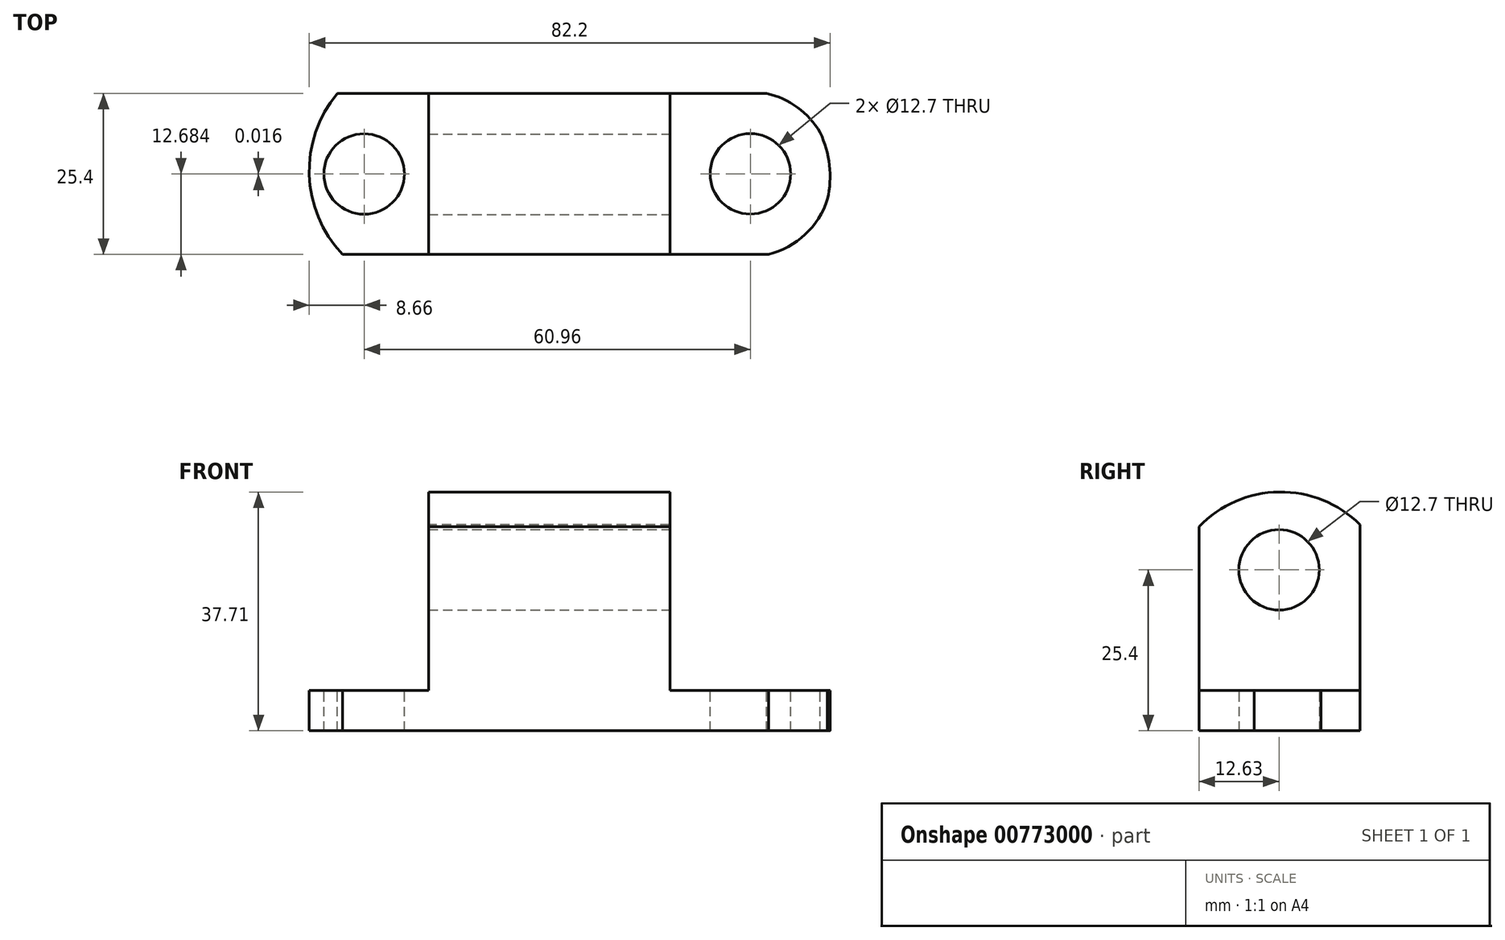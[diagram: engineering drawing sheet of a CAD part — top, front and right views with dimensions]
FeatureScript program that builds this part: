
annotation { "Feature Type Name" : "Feature", "Feature Type Description" : "" }
export const myFeature = defineFeature(function(context is Context, id is Id, definition is map)
    precondition{}
    {
        {
            var Q0;
            Q0=qCreatedBy(makeId("Front.planeOp"),FACE);
            var sketch = newSketch(context, id + "F0", { "sketchPlane" : qUnion([Q0])});
            skLineSegment(sketch, "E0", {"start": v(0, 0) * mm, "end": v(82.55, 0) * mm});
            skLineSegment(sketch, "E1", {"start": v(82.55, 0) * mm, "end": v(82.55, 38.1) * mm});
            skLineSegment(sketch, "E2", {"start": v(82.55, 38.1) * mm, "end": v(0, 38.1) * mm});
            skLineSegment(sketch, "E3", {"start": v(0, 38.1) * mm, "end": v(0, 0) * mm});
            skSolve(sketch);
        }
        {
            var Q0;
            Q0=makeQuery(id+"F0.imprint","IMPRINT",FACE,{"disambiguationData":[TD([[makeQuery(id+"F0.imprint","IMPRINT",EDGE,{"derivedFrom":sQuery(id+"F0.wireOp",EDGE,"E0")}),1.0]])]});
            extrude(context, id + "F1", {"entities" : qUnion([Q0]), "depth" : 25.4 * mm, "offsetDistance" : 25.4 * mm});
        }
        {
            var Q0;
            Q0=makeQuery(id+"F1.opExtrude","CAP_FACE",FACE,{"disambiguationData":[OSD([sQuery(id+"F0.wireOp",EDGE,"E0"),sQuery(id+"F0.wireOp",EDGE,"E1"),sQuery(id+"F0.wireOp",EDGE,"E2"),sQuery(id+"F0.wireOp",EDGE,"E3")])],"isStart":false});
            var sketch = newSketch(context, id + "F2", { "sketchPlane" : qUnion([Q0])});
            skLineSegment(sketch, "E4", {"start": v(57.15, 38.1) * mm, "end": v(57.15, 6.35) * mm});
            skLineSegment(sketch, "E5", {"start": v(57.15, 6.35) * mm, "end": v(82.55, 6.35) * mm});
            skLineSegment(sketch, "E6", {"start": v(82.55, 6.35) * mm, "end": v(82.55, 38.1) * mm});
            skLineSegment(sketch, "E7", {"start": v(82.55, 38.1) * mm, "end": v(57.15, 38.1) * mm});
            skSolve(sketch);
        }
        {
            var Q0;
            Q0=makeQuery(id+"F2.imprint","IMPRINT",FACE,{"disambiguationData":[TD([[makeQuery(id+"F2.imprint","IMPRINT",EDGE,{"derivedFrom":sQuery(id+"F2.wireOp",EDGE,"E4")}),1.0]])]});
            extrude(context, id + "F3", {"entities" : qUnion([Q0]), "operationType" : NewBodyOperationType.REMOVE, "oppositeDirection" : true, "depth" : 25.4 * mm, "offsetDistance" : 25.4 * mm});
        }
        {
            var Q0;
            Q0=makeQuery(id+"F1.opExtrude","CAP_FACE",FACE,{"disambiguationData":[OSD([sQuery(id+"F0.wireOp",EDGE,"E0"),sQuery(id+"F0.wireOp",EDGE,"E1"),sQuery(id+"F0.wireOp",EDGE,"E2"),sQuery(id+"F0.wireOp",EDGE,"E3")])],"isStart":false});
            var sketch = newSketch(context, id + "F4", { "sketchPlane" : qUnion([Q0])});
            skLineSegment(sketch, "E8", {"start": v(19.05, 38.1) * mm, "end": v(19.05, 6.35) * mm});
            skLineSegment(sketch, "E9", {"start": v(19.05, 6.35) * mm, "end": v(0, 6.35) * mm});
            skLineSegment(sketch, "E10", {"start": v(0, 6.35) * mm, "end": v(0, 38.1) * mm});
            skLineSegment(sketch, "E11", {"start": v(0, 38.1) * mm, "end": v(19.05, 38.1) * mm});
            skSolve(sketch);
        }
        {
            var Q0;
            Q0=makeQuery(id+"F4.imprint","IMPRINT",FACE,{"disambiguationData":[TD([[makeQuery(id+"F4.imprint","IMPRINT",EDGE,{"derivedFrom":sQuery(id+"F4.wireOp",EDGE,"E8")}),-1.0]])]});
            extrude(context, id + "F5", {"entities" : qUnion([Q0]), "operationType" : NewBodyOperationType.REMOVE, "oppositeDirection" : true, "depth" : 25.4 * mm, "offsetDistance" : 25.4 * mm});
        }
        {
            var Q0;
            Q0=makeQuery(id+"F3.boolean.opBoolean","COPY",FACE,{"derivedFrom":makeQuery(id+"F3.opExtrude","SWEPT_FACE",FACE,{"disambiguationData":[OSD([sQuery(id+"F2.wireOp",EDGE,"E5")])]})});
            var sketch = newSketch(context, id + "F6", { "sketchPlane" : qUnion([Q0])});
            skCircle(sketch, "E12", {"center": v(69.85, -12.7) * mm, "radius": 6.35 * mm});
            skSolve(sketch);
        }
        {
            var Q0;
            Q0=makeQuery(id+"F6.imprint","IMPRINT",FACE,{"disambiguationData":[TD([[makeQuery(id+"F6.imprint","IMPRINT",EDGE,{"derivedFrom":sQuery(id+"F6.wireOp",EDGE,"E12")}),1.0]])]});
            extrude(context, id + "F7", {"entities" : qUnion([Q0]), "operationType" : NewBodyOperationType.REMOVE, "oppositeDirection" : true, "depth" : 25.4 * mm, "offsetDistance" : 25.4 * mm});
        }
        {
            var Q0;
            Q0=makeQuery(id+"F5.boolean.opBoolean","COPY",FACE,{"derivedFrom":makeQuery(id+"F5.opExtrude","SWEPT_FACE",FACE,{"disambiguationData":[OSD([sQuery(id+"F4.wireOp",EDGE,"E9")])]})});
            var sketch = newSketch(context, id + "F8", { "sketchPlane" : qUnion([Q0])});
            skCircle(sketch, "E13", {"center": v(8.9, -12.72) * mm, "radius": 6.35 * mm});
            skSolve(sketch);
        }
        {
            var Q0;
            Q0=makeQuery(id+"F8.imprint","IMPRINT",FACE,{"disambiguationData":[TD([[makeQuery(id+"F8.imprint","IMPRINT",EDGE,{"derivedFrom":sQuery(id+"F8.wireOp",EDGE,"E13")}),1.0]])]});
            extrude(context, id + "F9", {"entities" : qUnion([Q0]), "operationType" : NewBodyOperationType.REMOVE, "oppositeDirection" : true, "depth" : 25.4 * mm, "offsetDistance" : 25.4 * mm});
        }
        {
            var Q0;
            Q0=makeQuery(id+"F5.boolean.opBoolean","COPY",FACE,{"derivedFrom":makeQuery(id+"F5.opExtrude","SWEPT_FACE",FACE,{"disambiguationData":[OSD([sQuery(id+"F4.wireOp",EDGE,"E8")])]})});
            var sketch = newSketch(context, id + "F10", { "sketchPlane" : qUnion([Q0])});
            skArc(sketch, "E14", {"start": v(25.4, 32.2) * mm, "mid": v(12.77, 37.7) * mm, "end": v(0, 32.54) * mm});
            skSolve(sketch);
        }
        {
            var Q0;
            {var subQ0=sQuery(id+"F10.wireOp",EDGE,"E14");Q0=makeQuery(id+"F10.imprint","IMPRINT",FACE,{"disambiguationData":[TD([[makeQuery(id+"F10.imprint","IMPRINT",EDGE,{"derivedFrom":subQ0}),-1.0]])]});}
            extrude(context, id + "F11", {"entities" : qUnion([Q0]), "operationType" : NewBodyOperationType.REMOVE, "oppositeDirection" : true, "depth" : 38.1 * mm, "offsetDistance" : 25.4 * mm});
        }
        {
            var Q0;
            Q0=makeQuery(id+"F3.boolean.opBoolean","COPY",FACE,{"derivedFrom":makeQuery(id+"F3.opExtrude","SWEPT_FACE",FACE,{"disambiguationData":[OSD([sQuery(id+"F2.wireOp",EDGE,"E4")])]})});
            var sketch = newSketch(context, id + "F12", { "sketchPlane" : qUnion([Q0])});
            skCircle(sketch, "E15", {"center": v(-12.77, 25.4) * mm, "radius": 6.35 * mm});
            skPoint(sketch, "E15.centerSnap0", {"position": v(-12.77, 37.7) * mm});
            skSolve(sketch);
        }
        {
            var Q0;
            Q0=makeQuery(id+"F12.imprint","IMPRINT",FACE,{"disambiguationData":[TD([[makeQuery(id+"F12.imprint","IMPRINT",EDGE,{"derivedFrom":sQuery(id+"F12.wireOp",EDGE,"E15")}),1.0]])]});
            extrude(context, id + "F13", {"entities" : qUnion([Q0]), "operationType" : NewBodyOperationType.REMOVE, "oppositeDirection" : true, "depth" : 50.8 * mm, "offsetDistance" : 25.4 * mm});
        }
        {
            var Q0;
            Q0=makeQuery(id+"F5.boolean.opBoolean","COPY",FACE,{"derivedFrom":makeQuery(id+"F5.opExtrude","SWEPT_FACE",FACE,{"disambiguationData":[OSD([sQuery(id+"F4.wireOp",EDGE,"E9")])]})});
            var sketch = newSketch(context, id + "F14", { "sketchPlane" : qUnion([Q0])});
            skArc(sketch, "E16", {"start": v(4.65, 0) * mm, "mid": v(0.24, -12.86) * mm, "end": v(5.48, -25.4) * mm});
            skSolve(sketch);
        }
        {
            var Q0;
            {var subQ0=sQuery(id+"F14.wireOp",EDGE,"E16");Q0=makeQuery(id+"F14.imprint","IMPRINT",FACE,{"disambiguationData":[TD([[makeQuery(id+"F14.imprint","IMPRINT",EDGE,{"derivedFrom":subQ0}),-1.0]])]});}
            extrude(context, id + "F15", {"entities" : qUnion([Q0]), "operationType" : NewBodyOperationType.REMOVE, "oppositeDirection" : true, "depth" : 50.8 * mm, "offsetDistance" : 25.4 * mm});
        }
        {
            var Q0;
            Q0=makeQuery(id+"F3.boolean.opBoolean","COPY",FACE,{"derivedFrom":makeQuery(id+"F3.opExtrude","SWEPT_FACE",FACE,{"disambiguationData":[OSD([sQuery(id+"F2.wireOp",EDGE,"E5")])]})});
            var sketch = newSketch(context, id + "F16", { "sketchPlane" : qUnion([Q0])});
            skArc(sketch, "E17", {"start": v(76.78, -25.4) * mm, "mid": v(82.42, -12.45) * mm, "end": v(75.75, 0) * mm});
            skSolve(sketch);
        }
        {
            var Q0;
            {var subQ0=sQuery(id+"F16.wireOp",EDGE,"E17");Q0=makeQuery(id+"F16.imprint","IMPRINT",FACE,{"disambiguationData":[TD([[makeQuery(id+"F16.imprint","IMPRINT",EDGE,{"derivedFrom":subQ0}),-1.0]])]});}
            extrude(context, id + "F17", {"entities" : qUnion([Q0]), "operationType" : NewBodyOperationType.REMOVE, "oppositeDirection" : true, "depth" : 50.8 * mm, "offsetDistance" : 25.4 * mm});
        }
        {
            var Q0;
            Q0=makeQuery(id+"F3.boolean.opBoolean","COPY",FACE,{"derivedFrom":makeQuery(id+"F3.opExtrude","SWEPT_FACE",FACE,{"disambiguationData":[OSD([sQuery(id+"F2.wireOp",EDGE,"E5")])]})});
            var sketch = newSketch(context, id + "F18", { "sketchPlane" : qUnion([Q0])});
            skArc(sketch, "E18", {"start": v(72.74, -25.4) * mm, "mid": v(82.64, -12.58) * mm, "end": v(72.43, 0) * mm});
            skSolve(sketch);
        }
        {
            var Q0;
            {var subQ0=sQuery(id+"F18.wireOp",EDGE,"E18");var subQ1=makeQuery(id+"F3.boolean.opBoolean","COPY",EDGE,{"derivedFrom":makeQuery(id+"F3.opExtrude","CAP_EDGE",EDGE,{"disambiguationData":[OSD([sQuery(id+"F2.wireOp",EDGE,"E5")])],"isStart":false})});var subQ2=makeQuery(id+"F18.imprint","INTERSECT",VERTEX,{"derivedFrom":[subQ1,subQ0]});Q0=makeQuery(id+"F18.imprint","IMPRINT",FACE,{"disambiguationData":[TD([[makeQuery(id+"F18.imprint","IMPRINT",EDGE,{"disambiguationData":[TD([[subQ2,1.0]])],"derivedFrom":subQ0}),-1.0]])]});}
            extrude(context, id + "F19", {"entities" : qUnion([Q0]), "operationType" : NewBodyOperationType.REMOVE, "oppositeDirection" : true, "depth" : 25.4 * mm, "offsetDistance" : 25.4 * mm});
        }
    });
